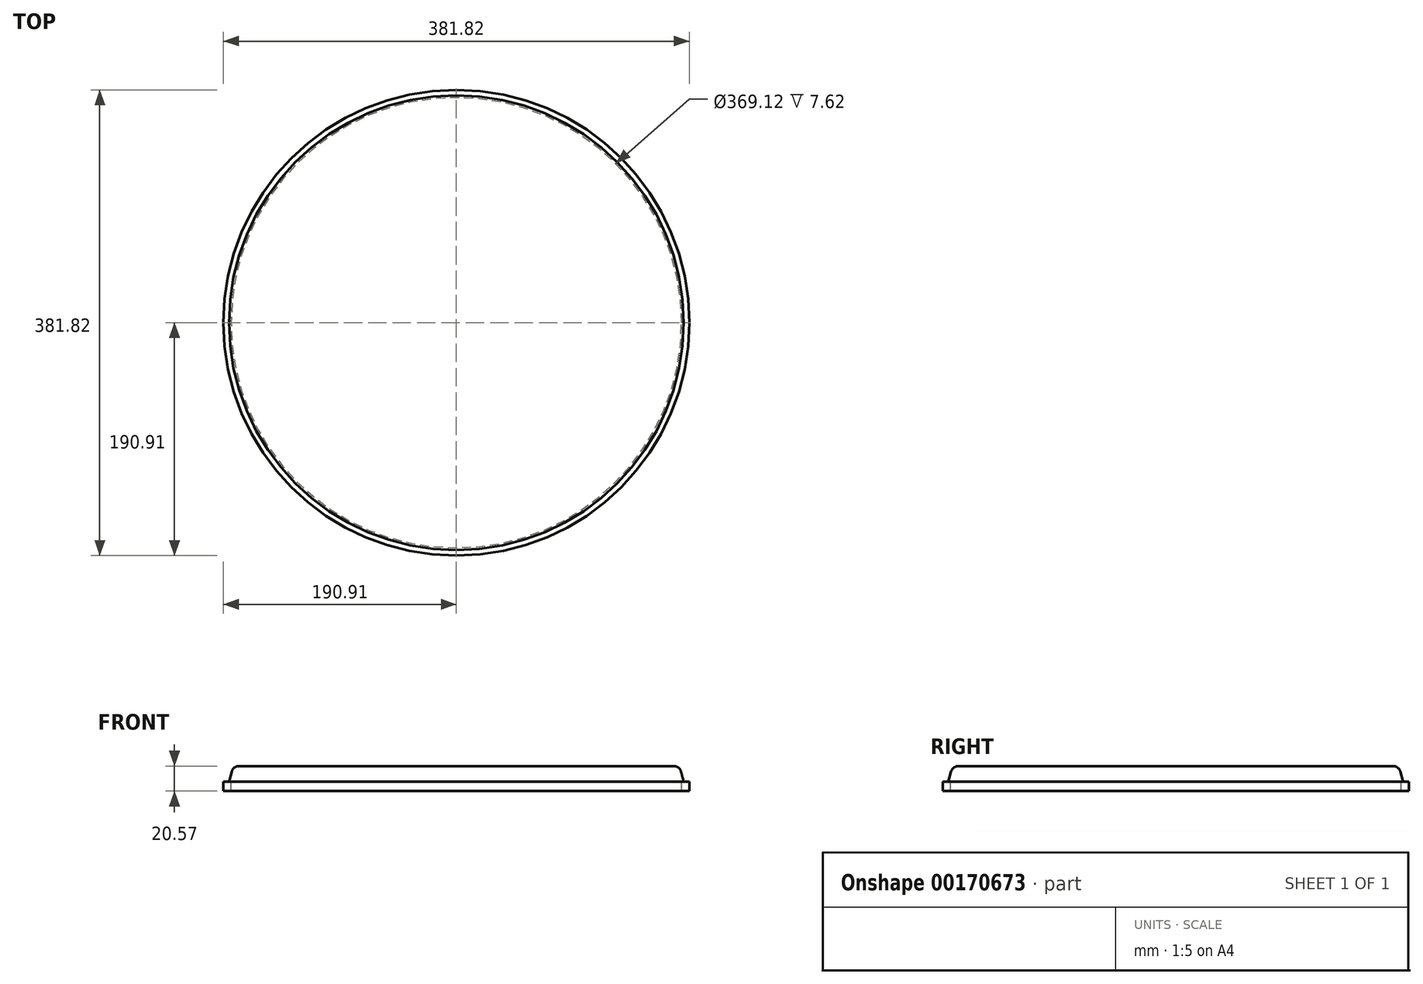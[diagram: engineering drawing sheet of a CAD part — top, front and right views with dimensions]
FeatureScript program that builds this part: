
annotation { "Feature Type Name" : "Feature", "Feature Type Description" : "" }
export const myFeature = defineFeature(function(context is Context, id is Id, definition is map)
    precondition{}
    {
        {
            var Q0;
            Q0=qCreatedBy(makeId("Front.planeOp"),FACE);
            var sketch = newSketch(context, id + "F0", { "sketchPlane" : qUnion([Q0])});
            skLineSegment(sketch, "E0", {"start": v(0, 0) * mm, "end": v(-177.8, 0) * mm});
            skLineSegment(sketch, "E1", {"start": v(-183.93, -4.7) * mm, "end": v(-186.08, -12.7) * mm});
            skLineSegment(sketch, "E2", {"start": v(-186.08, -12.7) * mm, "end": v(-184.56, -12.7) * mm});
            skLineSegment(sketch, "E3", {"start": v(-184.56, -12.7) * mm, "end": v(-184.56, -20.32) * mm});
            skLineSegment(sketch, "E4", {"start": v(-184.56, -20.32) * mm, "end": v(-190.91, -20.32) * mm});
            skLineSegment(sketch, "E5", {"start": v(-190.91, -20.32) * mm, "end": v(-190.91, -12.7) * mm});
            skLineSegment(sketch, "E6", {"start": v(-190.91, -12.7) * mm, "end": v(-186.34, -12.7) * mm});
            skLineSegment(sketch, "E7", {"start": v(-186.34, -12.7) * mm, "end": v(-184.13, -4.45) * mm});
            skLineSegment(sketch, "E8", {"start": v(-178, 0.25) * mm, "end": v(0, 0.25) * mm});
            skLineSegment(sketch, "E9", {"start": v(0, 0.25) * mm, "end": v(0, 0) * mm});
            skPoint(sketch, "E10.visualSharp", {"position": v(-182.87, 0.25) * mm});
            skArc(sketch, "E10.filletArc", {"start": v(-178, 0.25) * mm, "mid": v(-181.86, -1.06) * mm, "end": v(-184.13, -4.45) * mm});
            skPoint(sketch, "E11.visualSharp", {"position": v(-182.67, 0) * mm});
            skArc(sketch, "E11.filletArc", {"start": v(-177.8, 0) * mm, "mid": v(-181.67, -1.31) * mm, "end": v(-183.93, -4.7) * mm});
            skLineSegment(sketch, "E12", {"start": v(0, 0.25) * mm, "end": v(0, -92.5) * mm, "construction": true});
            skSolve(sketch);
        }
        {
            var Q0;
            Q0=makeQuery(id+"F0.imprint","IMPRINT",FACE,{"disambiguationData":[TD([[makeQuery(id+"F0.imprint","IMPRINT",EDGE,{"derivedFrom":sQuery(id+"F0.wireOp",EDGE,"E0")}),-1.0]])]});
            var Q1;
            Q1=sQuery(id+"F0.wireOp",EDGE,"E12");
            revolve(context, id + "F1", {"surfaceOperationType" : NewSurfaceOperationType.NEW, "entities" : qUnion([Q0]), "axis" : qUnion([Q1]), "revolveType" : RevolveType.FULL});
        }
    });
